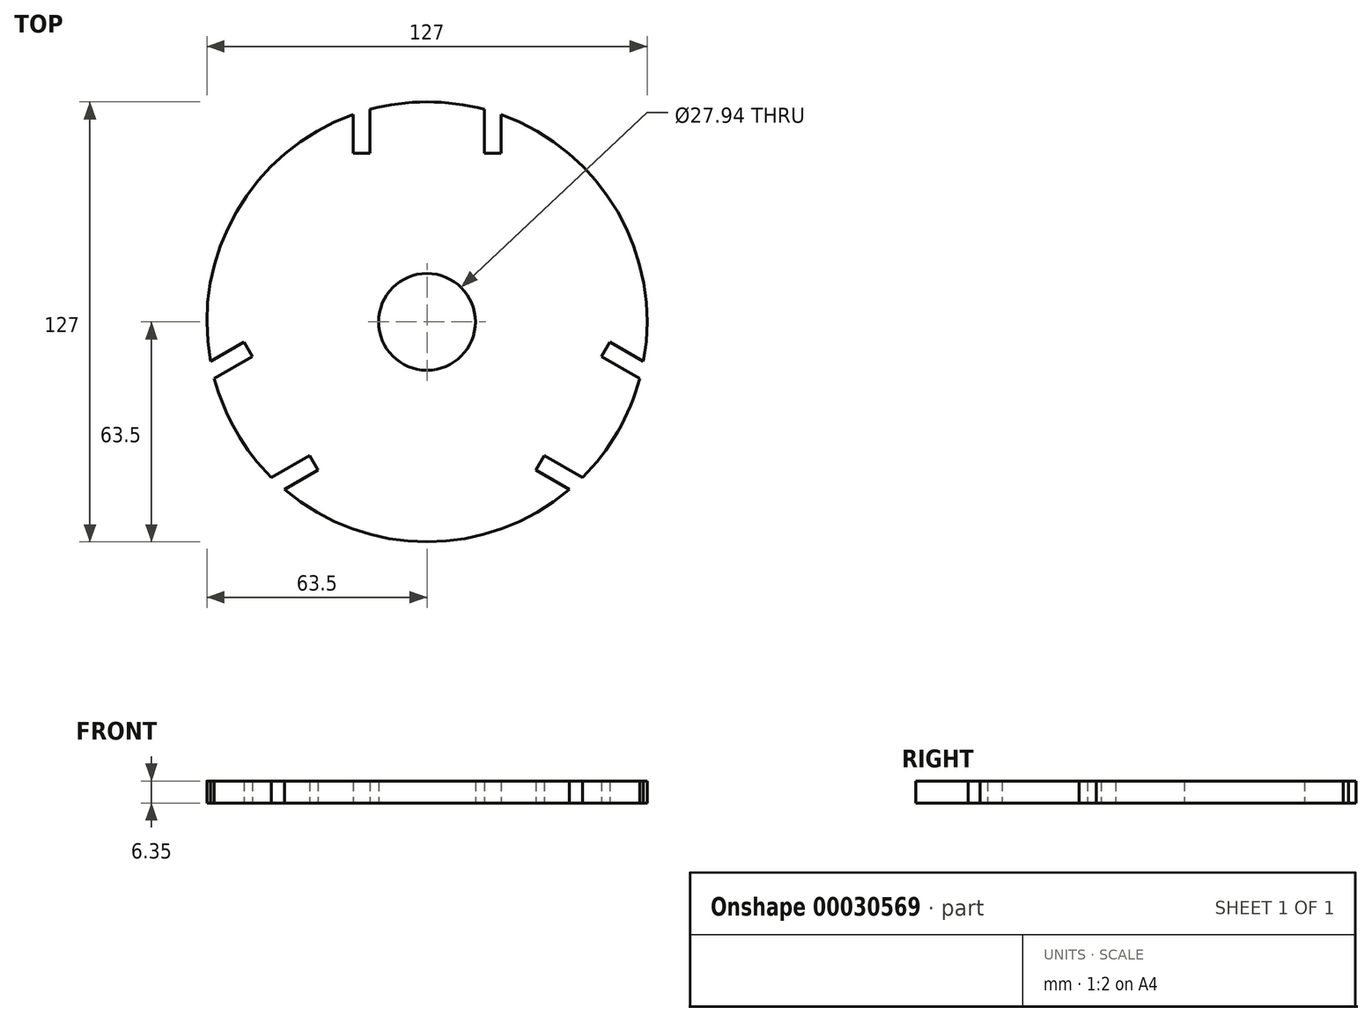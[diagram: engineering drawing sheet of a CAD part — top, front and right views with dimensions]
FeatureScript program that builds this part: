
annotation { "Feature Type Name" : "Feature", "Feature Type Description" : "" }
export const myFeature = defineFeature(function(context is Context, id is Id, definition is map)
    precondition{}
    {
        {
            var Q0;
            Q0=qCreatedBy(makeId("Top.planeOp"),FACE);
            var sketch = newSketch(context, id + "F0", { "sketchPlane" : qUnion([Q0])});
            skCircle(sketch, "E0", {"center": v(0, 0) * mm, "radius": 13.97 * mm});
            skArc(sketch, "E1", {"start": v(-21.34, 59.8) * mm, "mid": v(-55, 31.75) * mm, "end": v(-62.46, -11.43) * mm});
            skLineSegment(sketch, "E2", {"start": v(-16.51, 48.62) * mm, "end": v(-16.51, 61.32) * mm});
            skLineSegment(sketch, "E3", {"start": v(-16.51, 48.62) * mm, "end": v(-21.34, 48.62) * mm});
            skLineSegment(sketch, "E4", {"start": v(-21.34, 48.62) * mm, "end": v(-21.34, 59.8) * mm});
            skLineSegment(sketch, "E5.MirrorCS", {"start": v(16.51, 48.62) * mm, "end": v(16.51, 61.32) * mm});
            skLineSegment(sketch, "E6.MirrorCS", {"start": v(16.51, 48.62) * mm, "end": v(21.34, 48.62) * mm});
            skLineSegment(sketch, "E7.MirrorCS", {"start": v(21.34, 48.62) * mm, "end": v(21.34, 59.8) * mm});
            skArc(sketch, "E8.trimOffspring", {"start": v(16.51, 61.32) * mm, "mid": v(0, 63.5) * mm, "end": v(-16.51, 61.32) * mm});
            skLineSegment(sketch, "E9.1.0", {"start": v(-33.85, -38.6) * mm, "end": v(-44.85, -44.96) * mm});
            skLineSegment(sketch, "E9.1.1", {"start": v(-33.85, -38.6) * mm, "end": v(-31.43, -42.79) * mm});
            skLineSegment(sketch, "E9.1.2", {"start": v(-31.43, -42.79) * mm, "end": v(-41.13, -48.38) * mm});
            skLineSegment(sketch, "E9.1.3", {"start": v(-50.36, -10) * mm, "end": v(-61.36, -16.36) * mm});
            skLineSegment(sketch, "E9.1.4", {"start": v(-50.36, -10) * mm, "end": v(-52.77, -5.83) * mm});
            skLineSegment(sketch, "E9.1.5", {"start": v(-52.77, -5.83) * mm, "end": v(-62.46, -11.43) * mm});
            skLineSegment(sketch, "E9.2.0", {"start": v(50.36, -10) * mm, "end": v(61.36, -16.36) * mm});
            skLineSegment(sketch, "E9.2.1", {"start": v(50.36, -10) * mm, "end": v(52.77, -5.83) * mm});
            skLineSegment(sketch, "E9.2.2", {"start": v(52.77, -5.83) * mm, "end": v(62.46, -11.43) * mm});
            skLineSegment(sketch, "E9.2.3", {"start": v(33.85, -38.6) * mm, "end": v(44.85, -44.96) * mm});
            skLineSegment(sketch, "E9.2.4", {"start": v(33.85, -38.6) * mm, "end": v(31.43, -42.79) * mm});
            skLineSegment(sketch, "E9.2.5", {"start": v(31.43, -42.79) * mm, "end": v(41.13, -48.38) * mm});
            skArc(sketch, "E10.trimOffspring", {"start": v(62.46, -11.43) * mm, "mid": v(55, 31.75) * mm, "end": v(21.34, 59.8) * mm});
            skArc(sketch, "E11.trimOffspring", {"start": v(44.85, -44.96) * mm, "mid": v(55, -31.75) * mm, "end": v(61.36, -16.36) * mm});
            skArc(sketch, "E12.trimOffspring", {"start": v(-41.13, -48.38) * mm, "mid": v(0, -63.5) * mm, "end": v(41.13, -48.38) * mm});
            skArc(sketch, "E13.trimOffspring", {"start": v(-61.36, -16.36) * mm, "mid": v(-55, -31.75) * mm, "end": v(-44.85, -44.96) * mm});
            skSolve(sketch);
        }
        {
            var Q0;
            Q0 = qSketchRegion(id + "F0", true);
            extrude(context, id + "F1", {"entities" : qUnion([Q0]), "depth" : 6.35 * mm});
        }
    });
